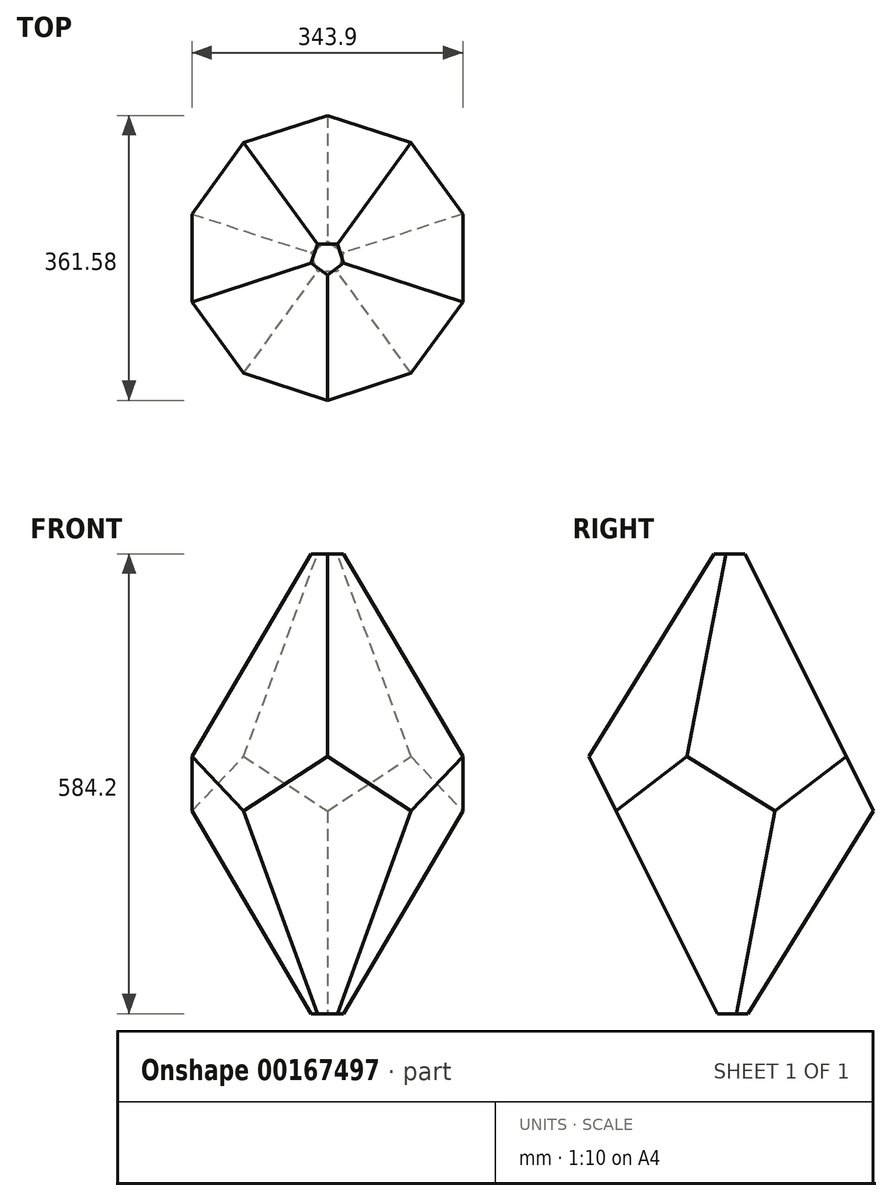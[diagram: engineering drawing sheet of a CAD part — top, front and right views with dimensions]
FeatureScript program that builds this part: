
annotation { "Feature Type Name" : "Feature", "Feature Type Description" : "" }
export const myFeature = defineFeature(function(context is Context, id is Id, definition is map)
    precondition{}
    {
        {
            var Q0;
            Q0=qCreatedBy(makeId("Top.planeOp"),FACE);
            var sketch = newSketch(context, id + "F0", { "sketchPlane" : qUnion([Q0])});
            skCircle(sketch, "E0.cCircle", {"center": v(0, 0) * mm, "radius": 17.48 * mm, "construction": true});
            skLineSegment(sketch, "E0.0", {"start": v(20.55, 6.68) * mm, "end": v(12.7, -17.48) * mm});
            skLineSegment(sketch, "E0.1", {"start": v(12.7, -17.48) * mm, "end": v(-12.7, -17.48) * mm});
            skLineSegment(sketch, "E0.2", {"start": v(-12.7, -17.48) * mm, "end": v(-20.55, 6.68) * mm});
            skLineSegment(sketch, "E0.3", {"start": v(-20.55, 6.68) * mm, "end": v(0, 21.6) * mm});
            skLineSegment(sketch, "E0.4", {"start": v(0, 21.6) * mm, "end": v(20.55, 6.68) * mm});
            skPoint(sketch, "E0.0.midPoint", {"position": v(16.62, -5.4) * mm});
            skSolve(sketch);
        }
        {
            var Q0;
            Q0=makeQuery(id+"F0.imprint","IMPRINT",FACE,{"disambiguationData":[TD([[makeQuery(id+"F0.imprint","IMPRINT",EDGE,{"derivedFrom":sQuery(id+"F0.wireOp",EDGE,"E0.0")}),-1.0]])]});
            extrude(context, id + "F1", {"entities" : qUnion([Q0]), "depth" : 584.2 * mm, "hasDraft" : true, "draftAngle" : acos(-1 / sqrt(5)) - 90 * degree});
        }
        {
            var Q0;
            Q0=makeQuery(id+"F1.opExtrude","CAP_FACE",FACE,{"disambiguationData":[OSD([sQuery(id+"F0.wireOp",EDGE,"E0.0"),sQuery(id+"F0.wireOp",EDGE,"E0.1"),sQuery(id+"F0.wireOp",EDGE,"E0.2"),sQuery(id+"F0.wireOp",EDGE,"E0.3"),sQuery(id+"F0.wireOp",EDGE,"E0.4")])],"isStart":false});
            var sketch = newSketch(context, id + "F2", { "sketchPlane" : qUnion([Q0])});
            skCircle(sketch, "E1.cCircle", {"center": v(0, 0) * mm, "radius": 17.48 * mm, "construction": true});
            skLineSegment(sketch, "E1.0", {"start": v(12.7, 17.48) * mm, "end": v(20.55, -6.68) * mm});
            skLineSegment(sketch, "E1.1", {"start": v(20.55, -6.68) * mm, "end": v(0, -21.6) * mm});
            skLineSegment(sketch, "E1.2", {"start": v(0, -21.6) * mm, "end": v(-20.55, -6.68) * mm});
            skLineSegment(sketch, "E1.3", {"start": v(-20.55, -6.68) * mm, "end": v(-12.7, 17.48) * mm});
            skLineSegment(sketch, "E1.4", {"start": v(-12.7, 17.48) * mm, "end": v(12.7, 17.48) * mm});
            skPoint(sketch, "E1.0.midPoint", {"position": v(16.62, 5.4) * mm});
            skSolve(sketch);
        }
        {
            var Q0;
            Q0=makeQuery(id+"F2.imprint","IMPRINT",FACE,{"disambiguationData":[TD([[makeQuery(id+"F2.imprint","IMPRINT",EDGE,{"derivedFrom":sQuery(id+"F2.wireOp",EDGE,"E1.0")}),1.0]])]});
            extrude(context, id + "F3", {"entities" : qUnion([Q0]), "operationType" : NewBodyOperationType.REMOVE, "endBound" : BoundingType.THROUGH_ALL, "oppositeDirection" : true, "depth" : 36.32 * mm, "hasDraft" : true, "draftAngle" : acos(-1 / sqrt(5)) - 90 * degree, "draftPullDirection" : true});
        }
    });
